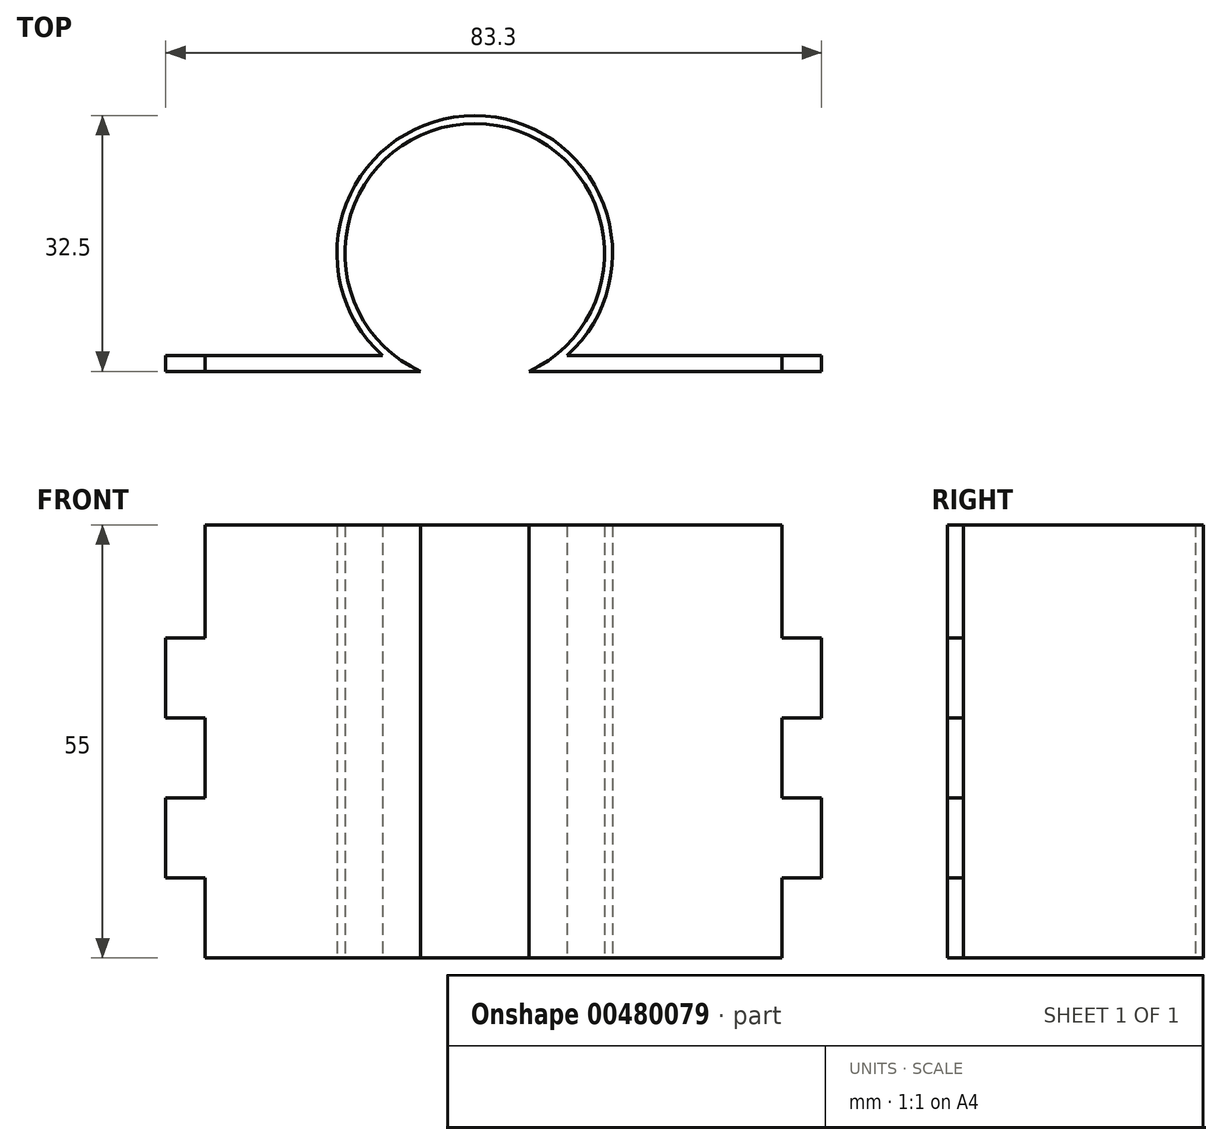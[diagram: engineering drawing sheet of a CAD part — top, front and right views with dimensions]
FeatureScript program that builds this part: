
annotation { "Feature Type Name" : "Feature", "Feature Type Description" : "" }
export const myFeature = defineFeature(function(context is Context, id is Id, definition is map)
    precondition{}
    {
        {
            var Q0;
            Q0=qCreatedBy(makeId("Front.planeOp"),FACE);
            var sketch = newSketch(context, id + "F0", { "sketchPlane" : qUnion([Q0])});
            skLineSegment(sketch, "E0", {"start": v(3.75, 0) * mm, "end": v(3.35, 0) * mm});
            skLineSegment(sketch, "E1", {"start": v(3.35, 0) * mm, "end": v(3.35, 55) * mm});
            skLineSegment(sketch, "E2", {"start": v(76.25, 0) * mm, "end": v(76.65, 0) * mm});
            skLineSegment(sketch, "E3", {"start": v(76.65, 0) * mm, "end": v(76.65, 55) * mm});
            skLineSegment(sketch, "E4", {"start": v(3.35, 0) * mm, "end": v(3.35, 10.16) * mm, "construction": true});
            skLineSegment(sketch, "E5", {"start": v(3.35, 10.16) * mm, "end": v(-1.65, 10.16) * mm});
            skLineSegment(sketch, "E6.top", {"start": v(3.35, 20.32) * mm, "end": v(-1.65, 20.32) * mm});
            skLineSegment(sketch, "E6.left", {"start": v(3.35, 10.16) * mm, "end": v(3.35, 20.32) * mm});
            skLineSegment(sketch, "E6.right", {"start": v(-1.65, 10.16) * mm, "end": v(-1.65, 20.32) * mm});
            skLineSegment(sketch, "E7", {"start": v(3.35, 20.32) * mm, "end": v(3.35, 30.48) * mm, "construction": true});
            skLineSegment(sketch, "E8.bottom", {"start": v(3.35, 30.48) * mm, "end": v(-1.65, 30.48) * mm});
            skLineSegment(sketch, "E8.top", {"start": v(3.35, 40.64) * mm, "end": v(-1.65, 40.64) * mm});
            skLineSegment(sketch, "E8.left", {"start": v(3.35, 30.48) * mm, "end": v(3.35, 40.64) * mm});
            skLineSegment(sketch, "E8.right", {"start": v(-1.65, 30.48) * mm, "end": v(-1.65, 40.64) * mm});
            skLineSegment(sketch, "E9", {"start": v(76.65, 0) * mm, "end": v(76.65, 10.16) * mm, "construction": true});
            skLineSegment(sketch, "E10.bottom", {"start": v(76.65, 10.16) * mm, "end": v(81.65, 10.16) * mm});
            skLineSegment(sketch, "E10.top", {"start": v(76.65, 20.32) * mm, "end": v(81.65, 20.32) * mm});
            skLineSegment(sketch, "E10.left", {"start": v(76.65, 10.16) * mm, "end": v(76.65, 20.32) * mm});
            skLineSegment(sketch, "E10.right", {"start": v(81.65, 10.16) * mm, "end": v(81.65, 20.32) * mm});
            skLineSegment(sketch, "E11", {"start": v(76.65, 20.32) * mm, "end": v(76.65, 30.48) * mm, "construction": true});
            skLineSegment(sketch, "E12.bottom", {"start": v(76.65, 30.48) * mm, "end": v(81.65, 30.48) * mm});
            skLineSegment(sketch, "E12.top", {"start": v(76.65, 40.64) * mm, "end": v(81.65, 40.64) * mm});
            skLineSegment(sketch, "E12.left", {"start": v(76.65, 30.48) * mm, "end": v(76.65, 40.64) * mm});
            skLineSegment(sketch, "E12.right", {"start": v(81.65, 30.48) * mm, "end": v(81.65, 40.64) * mm});
            skLineSegment(sketch, "E13", {"start": v(3.35, 55) * mm, "end": v(76.65, 55) * mm});
            skLineSegment(sketch, "E14", {"start": v(3.35, 0) * mm, "end": v(76.65, 0) * mm});
            skSolve(sketch);
        }
        {
            var Q0;
            Q0 = qSketchRegion(id + "F0", true);
            extrude(context, id + "F1", {"entities" : qUnion([Q0]), "oppositeDirection" : true, "depth" : 2 * mm});
        }
        {
            var Q0;
            Q0=qCreatedBy(makeId("Top.planeOp"),FACE);
            var sketch = newSketch(context, id + "F2", { "sketchPlane" : qUnion([Q0])});
            skLineSegment(sketch, "E15", {"start": v(0, 0) * mm, "end": v(37.6, 0) * mm, "construction": true});
            skLineSegment(sketch, "E16", {"start": v(37.6, 0) * mm, "end": v(37.6, 15) * mm, "construction": true});
            skCircle(sketch, "E17", {"center": v(37.6, 15) * mm, "radius": 16.5 * mm});
            skLineSegment(sketch, "E18", {"start": v(37.6, 0) * mm, "end": v(37.6, 2) * mm, "construction": true});
            skLineSegment(sketch, "E19", {"start": v(37.6, 2) * mm, "end": v(47.77, 2) * mm});
            skLineSegment(sketch, "E20", {"start": v(37.6, 2) * mm, "end": v(27.45, 2) * mm});
            skCircle(sketch, "E21", {"center": v(37.6, 15) * mm, "radius": 17.5 * mm});
            skLineSegment(sketch, "E22", {"start": v(37.6, 2) * mm, "end": v(25.9, 2) * mm});
            skLineSegment(sketch, "E23", {"start": v(37.6, 2) * mm, "end": v(49.32, 2) * mm});
            skLineSegment(sketch, "E24", {"start": v(37.6, 0) * mm, "end": v(44.48, 0) * mm});
            skLineSegment(sketch, "E25", {"start": v(37.6, 0) * mm, "end": v(30.73, 0) * mm});
            skSolve(sketch);
        }
        {
            var Q0;
            {var subQ0=sQuery(id+"F2.wireOp",EDGE,"E22");var subQ1=sQuery(id+"F2.wireOp",EDGE,"E17");var subQ2=makeQuery(id+"F2.imprint","INTERSECT",VERTEX,{"derivedFrom":[subQ1,subQ0]});Q0=makeQuery(id+"F2.imprint","IMPRINT",FACE,{"disambiguationData":[TD([[makeQuery(id+"F2.imprint","IMPRINT",EDGE,{"disambiguationData":[TD([[subQ2,1.0]])],"derivedFrom":subQ1}),-1.0]])]});}
            extrude(context, id + "F3", {"entities" : qUnion([Q0]), "operationType" : NewBodyOperationType.ADD, "depth" : 55 * mm});
        }
        {
            var Q0;
            {var subQ6=sQuery(id+"F2.wireOp",EDGE,"E24");Q0=makeQuery(id+"F2.imprint","IMPRINT",FACE,{"disambiguationData":[TD([[makeQuery(id+"F2.imprint","IMPRINT",EDGE,{"derivedFrom":subQ6}),1.0]])]});}
            extrude(context, id + "F4", {"entities" : qUnion([Q0]), "operationType" : NewBodyOperationType.REMOVE, "depth" : 55 * mm});
        }
    });
